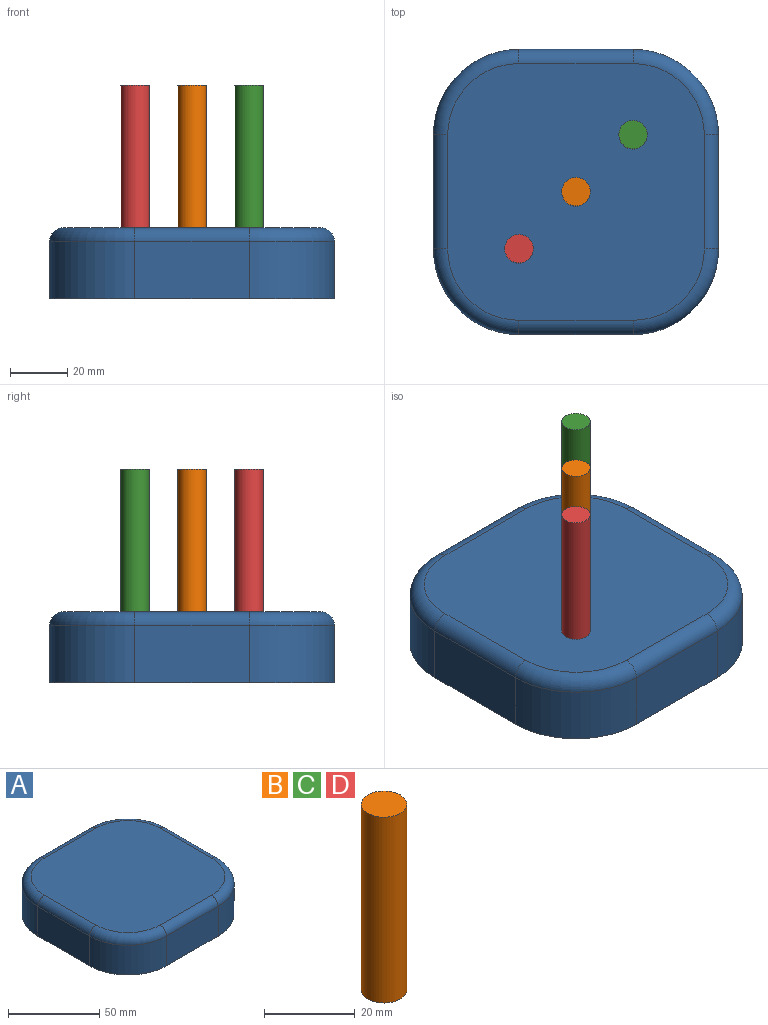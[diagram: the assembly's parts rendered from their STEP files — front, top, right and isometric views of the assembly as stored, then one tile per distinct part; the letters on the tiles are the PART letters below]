
ASSEMBLY  parts=4 mates=3
PART A: 18 faces, bbox 104.9x104.9x25 mm
  f0: plane 40x20mm, normal (0,1,0), area 800mm2, adj f1,f7,f9,f14
  f1: cylinder r=30mm len=30mm, axis (0,0,-1), area 942.5mm2, adj f0,f2,f9,f12
  f2: plane 40x20mm, normal (-1,0,0), area 800mm2, adj f1,f3,f9,f10
  f3: cylinder r=30mm len=30mm, axis (0,0,-1), area 942.5mm2, adj f2,f4,f9,f11
  f4: plane 40x20mm, normal (0,-1,0), area 800mm2, adj f3,f5,f9,f13
  f5: cylinder r=30mm len=30mm, axis (0,0,-1), area 942.5mm2, adj f4,f6,f9,f15
  f6: plane 40x20mm, normal (1,0,0), area 800mm2, adj f5,f7,f9,f17
  f7: cylinder r=30mm len=30mm, axis (0,0,-1), area 942.5mm2, adj f0,f6,f9,f16
  f8: plane 90x90mm, normal (0,0,1), area 7563.5mm2, adj f10,f11,f12,f13,f14,f15,f16,f17
  f9: plane 100x100mm, normal (0,0,-1), area 9227.4mm2, adj f0,f1,f2,f3,f4,f5,f6,f7
  f10: cylinder r=5mm len=40mm, axis (0,1,0), area 314.2mm2, adj f2,f8,f11,f12
  f11: torus R=25mm, axis (0,0,1), area 347.7mm2, adj f3,f8,f10,f13
  f12: torus R=25mm, axis (0,0,1), area 347.7mm2, adj f1,f8,f10,f14
  f13: cylinder r=5mm len=40mm, axis (-1,0,0), area 314.2mm2, adj f4,f8,f11,f15
  f14: cylinder r=5mm len=40mm, axis (1,0,0), area 314.2mm2, adj f0,f8,f12,f16
  f15: torus R=25mm, axis (0,0,1), area 347.7mm2, adj f5,f8,f13,f17
  f16: torus R=25mm, axis (0,0,1), area 347.7mm2, adj f7,f8,f14,f17
  f17: cylinder r=5mm len=40mm, axis (0,-1,0), area 314.2mm2, adj f6,f8,f15,f16
PART B: 3 faces, bbox 10x10x50 mm
  f0: cylinder r=5mm len=50mm, axis (0,0,-1), area 1570.8mm2, adj f1,f2
  f1: plane 10x10mm, normal (0,0,1), area 78.5mm2, adj f0
  f2: plane 10x10mm, normal (0,0,-1), area 78.5mm2, adj f0
PART C: same geometry as B
PART D: same geometry as B
PLACE A t=(-105.54,127.01,53.51)mm
PLACE B t=(-105.54,127.01,78.51)mm
PLACE C t=(-85.54,147.01,78.51)mm
PLACE D t=(-125.54,107.01,78.51)mm
MATE fastened C.f0 <-> A.f7  axis (0,0,-1) through (-85.54,147.01,78.51)mm
MATE fastened D.f0 <-> A.f3  axis (0,0,-1) through (-125.54,107.01,78.51)mm
MATE fastened B.f0 <-> A.f8  axis (0,0,-1) through (-105.54,127.01,78.51)mm
